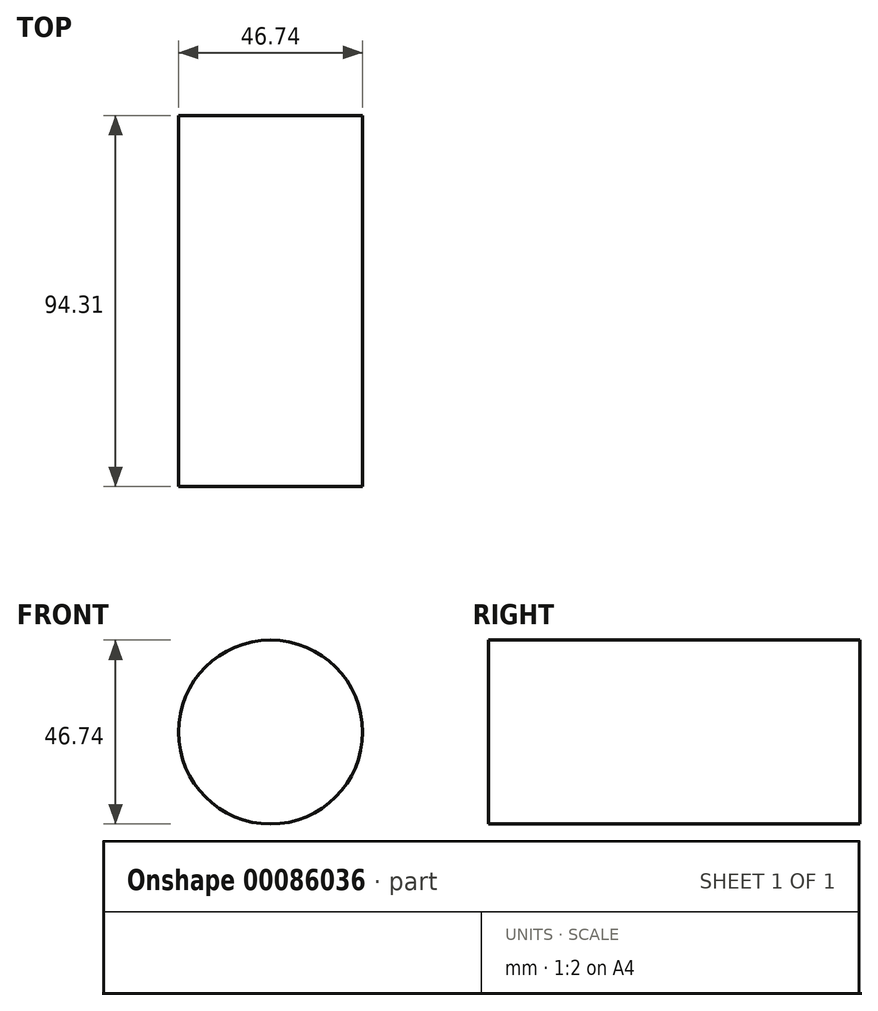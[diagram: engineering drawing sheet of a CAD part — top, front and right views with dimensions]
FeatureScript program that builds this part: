
annotation { "Feature Type Name" : "Feature", "Feature Type Description" : "" }
export const myFeature = defineFeature(function(context is Context, id is Id, definition is map)
    precondition{}
    {
        {
            var Q0;
            Q0=qCreatedBy(makeId("Front.planeOp"),FACE);
            var sketch = newSketch(context, id + "F0", { "sketchPlane" : qUnion([Q0])});
            skCircle(sketch, "E0", {"center": v(0, 0) * mm, "radius": 23.37 * mm});
            skSolve(sketch);
        }
        {
            var Q0;
            Q0=makeQuery(id+"F0.imprint","IMPRINT",FACE,{"disambiguationData":[TD([[makeQuery(id+"F0.imprint","IMPRINT",EDGE,{"derivedFrom":sQuery(id+"F0.wireOp",EDGE,"E0")}),1.0]])]});
            extrude(context, id + "F1", {"entities" : qUnion([Q0]), "depth" : 94.31 * mm});
        }
    });
